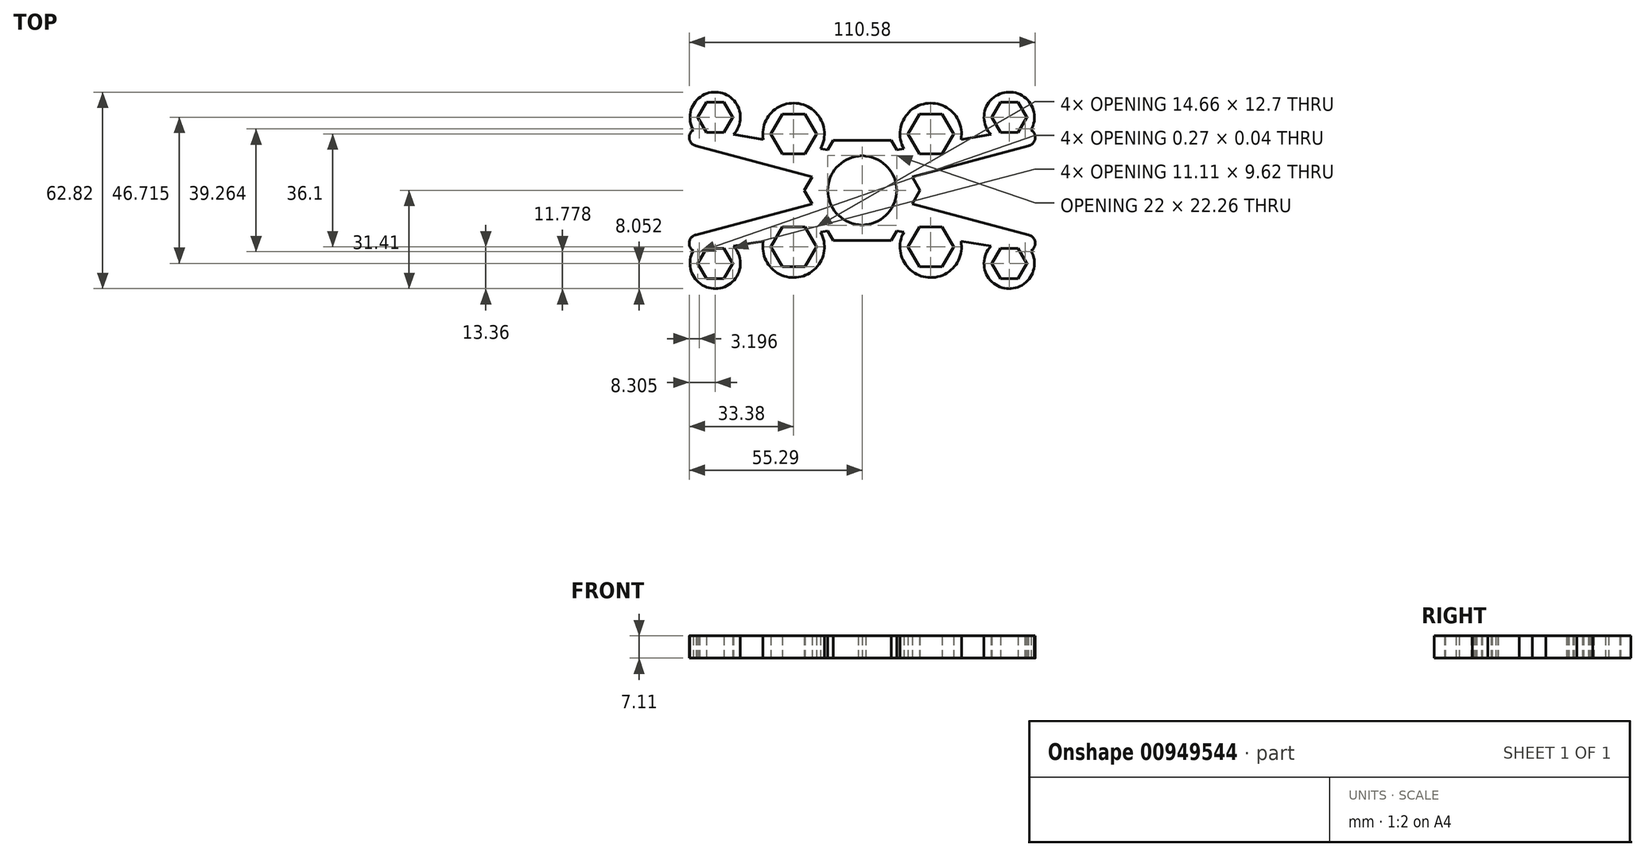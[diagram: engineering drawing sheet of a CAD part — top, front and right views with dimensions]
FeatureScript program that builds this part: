
annotation { "Feature Type Name" : "Feature", "Feature Type Description" : "" }
export const myFeature = defineFeature(function(context is Context, id is Id, definition is map)
    precondition{}
    {
        {
            var Q0;
            Q0=qCreatedBy(makeId("Top.planeOp"),FACE);
            var sketch = newSketch(context, id + "F0", { "sketchPlane" : qUnion([Q0])});
            skCircle(sketch, "E0", {"center": v(0, 0) * mm, "radius": 11 * mm});
            skCircle(sketch, "E1.cCircle", {"center": v(0, 0) * mm, "radius": 16 * mm, "construction": true});
            skLineSegment(sketch, "E1.0", {"start": v(18.48, 0) * mm, "end": v(9.24, -16) * mm});
            skLineSegment(sketch, "E1.1", {"start": v(9.24, -16) * mm, "end": v(-9.24, -16) * mm});
            skLineSegment(sketch, "E1.2", {"start": v(-9.24, -16) * mm, "end": v(-18.48, 0) * mm});
            skLineSegment(sketch, "E1.3", {"start": v(-18.48, 0) * mm, "end": v(-9.24, 16) * mm});
            skLineSegment(sketch, "E1.4", {"start": v(-9.24, 16) * mm, "end": v(9.24, 16) * mm});
            skLineSegment(sketch, "E1.5", {"start": v(9.24, 16) * mm, "end": v(18.48, 0) * mm});
            skPoint(sketch, "E1.0.midPoint", {"position": v(13.86, -8) * mm});
            skLineSegment(sketch, "E2", {"start": v(0, 0) * mm, "end": v(53.37, 14.3) * mm});
            skLineSegment(sketch, "E3", {"start": v(53.37, 14.3) * mm, "end": v(0, 0) * mm});
            skLineSegment(sketch, "E4", {"start": v(18.48, 0) * mm, "end": v(0, 0) * mm, "construction": true});
            skLineSegment(sketch, "E5", {"start": v(56.9, 20.41) * mm, "end": v(-2.32, 10.75) * mm});
            skLineSegment(sketch, "E6", {"start": v(57.96, 15.53) * mm, "end": v(56.9, 20.41) * mm});
            skArc(sketch, "E7", {"start": v(53.13, 14.24) * mm, "mid": v(55.22, 17.5) * mm, "end": v(51.96, 19.6) * mm});
            skCircle(sketch, "E8.cCircle", {"center": v(21.91, 18.05) * mm, "radius": 7.33 * mm, "construction": true});
            skLineSegment(sketch, "E8.0", {"start": v(25.58, 11.7) * mm, "end": v(18.24, 11.7) * mm});
            skLineSegment(sketch, "E8.1", {"start": v(18.24, 11.7) * mm, "end": v(14.58, 18.05) * mm});
            skLineSegment(sketch, "E8.2", {"start": v(14.58, 18.05) * mm, "end": v(18.24, 24.4) * mm});
            skLineSegment(sketch, "E8.3", {"start": v(18.24, 24.4) * mm, "end": v(25.58, 24.4) * mm});
            skLineSegment(sketch, "E8.4", {"start": v(25.58, 24.4) * mm, "end": v(29.24, 18.05) * mm});
            skLineSegment(sketch, "E8.5", {"start": v(29.24, 18.05) * mm, "end": v(25.58, 11.7) * mm});
            skCircle(sketch, "E9.0", {"center": v(21.91, 18.05) * mm, "radius": 9.83 * mm});
            skCircle(sketch, "E10.cCircle", {"center": v(46.99, 23.36) * mm, "radius": 5.56 * mm, "construction": true});
            skLineSegment(sketch, "E10.0", {"start": v(49.76, 18.55) * mm, "end": v(44.2, 18.55) * mm});
            skLineSegment(sketch, "E10.1", {"start": v(44.2, 18.55) * mm, "end": v(41.43, 23.36) * mm});
            skLineSegment(sketch, "E10.2", {"start": v(41.43, 23.36) * mm, "end": v(44.2, 28.17) * mm});
            skLineSegment(sketch, "E10.3", {"start": v(44.2, 28.17) * mm, "end": v(49.76, 28.17) * mm});
            skLineSegment(sketch, "E10.4", {"start": v(49.76, 28.17) * mm, "end": v(52.54, 23.36) * mm});
            skLineSegment(sketch, "E10.5", {"start": v(52.54, 23.36) * mm, "end": v(49.76, 18.55) * mm});
            skCircle(sketch, "E11.0", {"center": v(46.99, 23.36) * mm, "radius": 8.06 * mm});
            skLineSegment(sketch, "E12", {"start": v(0, 16) * mm, "end": v(0, -16) * mm, "construction": true});
            skLineSegment(sketch, "E13", {"start": v(-18.48, 0) * mm, "end": v(18.48, 0) * mm, "construction": true});
            skLineSegment(sketch, "E14.MirrorCS", {"start": v(14.58, -18.05) * mm, "end": v(18.24, -24.4) * mm});
            skLineSegment(sketch, "E15.MirrorCS", {"start": v(18.24, -24.4) * mm, "end": v(25.58, -24.4) * mm});
            skLineSegment(sketch, "E16.MirrorCS", {"start": v(25.58, -24.4) * mm, "end": v(29.24, -18.05) * mm});
            skLineSegment(sketch, "E17.MirrorCS", {"start": v(56.9, -20.41) * mm, "end": v(-2.32, -10.75) * mm});
            skLineSegment(sketch, "E18.MirrorCS", {"start": v(29.24, -18.05) * mm, "end": v(25.58, -11.7) * mm});
            skLineSegment(sketch, "E19.MirrorCS", {"start": v(25.58, -11.7) * mm, "end": v(18.24, -11.7) * mm});
            skLineSegment(sketch, "E20.MirrorCS", {"start": v(18.24, -11.7) * mm, "end": v(14.58, -18.05) * mm});
            skCircle(sketch, "E21.MirrorC", {"center": v(21.91, -18.05) * mm, "radius": 9.83 * mm});
            skLineSegment(sketch, "E22.MirrorCS", {"start": v(0, 0) * mm, "end": v(57.96, -15.53) * mm});
            skArc(sketch, "E23.MirrorCS", {"start": v(53.13, -14.24) * mm, "mid": v(55.22, -17.5) * mm, "end": v(51.96, -19.6) * mm});
            skLineSegment(sketch, "E24.MirrorCS", {"start": v(41.43, -23.36) * mm, "end": v(44.2, -28.17) * mm});
            skLineSegment(sketch, "E25.MirrorCS", {"start": v(44.2, -28.17) * mm, "end": v(49.76, -28.17) * mm});
            skLineSegment(sketch, "E26.MirrorCS", {"start": v(49.76, -28.17) * mm, "end": v(52.54, -23.36) * mm});
            skLineSegment(sketch, "E27.MirrorCS", {"start": v(52.54, -23.36) * mm, "end": v(49.76, -18.55) * mm});
            skCircle(sketch, "E28.MirrorC", {"center": v(46.99, -23.36) * mm, "radius": 5.56 * mm, "construction": true});
            skLineSegment(sketch, "E29.MirrorCS", {"start": v(49.76, -18.55) * mm, "end": v(44.2, -18.55) * mm});
            skLineSegment(sketch, "E30.MirrorCS", {"start": v(44.2, -18.55) * mm, "end": v(41.43, -23.36) * mm});
            skCircle(sketch, "E31.MirrorC", {"center": v(46.99, -23.36) * mm, "radius": 8.06 * mm});
            skLineSegment(sketch, "E32.MirrorCS", {"start": v(-25.58, -11.7) * mm, "end": v(-18.24, -11.7) * mm});
            skLineSegment(sketch, "E33.MirrorCS", {"start": v(-29.24, -18.05) * mm, "end": v(-25.58, -11.7) * mm});
            skLineSegment(sketch, "E34.MirrorCS", {"start": v(-18.24, -11.7) * mm, "end": v(-14.58, -18.05) * mm});
            skLineSegment(sketch, "E35.MirrorCS", {"start": v(-14.58, -18.05) * mm, "end": v(-18.24, -24.4) * mm});
            skLineSegment(sketch, "E36.MirrorCS", {"start": v(-18.24, -24.4) * mm, "end": v(-25.58, -24.4) * mm});
            skLineSegment(sketch, "E37.MirrorCS", {"start": v(-25.58, -24.4) * mm, "end": v(-29.24, -18.05) * mm});
            skCircle(sketch, "E38.MirrorC", {"center": v(-21.91, -18.05) * mm, "radius": 9.83 * mm});
            skLineSegment(sketch, "E39.MirrorCS", {"start": v(-56.9, -20.41) * mm, "end": v(2.32, -10.75) * mm});
            skLineSegment(sketch, "E40.MirrorCS", {"start": v(0, 0) * mm, "end": v(-57.96, -15.53) * mm});
            skLineSegment(sketch, "E41.MirrorCS", {"start": v(-49.76, -18.55) * mm, "end": v(-44.2, -18.55) * mm});
            skLineSegment(sketch, "E42.MirrorCS", {"start": v(-44.2, -18.55) * mm, "end": v(-41.43, -23.36) * mm});
            skLineSegment(sketch, "E43.MirrorCS", {"start": v(-52.54, -23.36) * mm, "end": v(-49.76, -18.55) * mm});
            skCircle(sketch, "E44.MirrorC", {"center": v(-46.99, -23.36) * mm, "radius": 5.56 * mm, "construction": true});
            skLineSegment(sketch, "E45.MirrorCS", {"start": v(-41.43, -23.36) * mm, "end": v(-44.2, -28.17) * mm});
            skLineSegment(sketch, "E46.MirrorCS", {"start": v(-44.2, -28.17) * mm, "end": v(-49.76, -28.17) * mm});
            skLineSegment(sketch, "E47.MirrorCS", {"start": v(-49.76, -28.17) * mm, "end": v(-52.54, -23.36) * mm});
            skArc(sketch, "E48.MirrorCS", {"start": v(-53.13, -14.24) * mm, "mid": v(-55.22, -17.5) * mm, "end": v(-51.96, -19.6) * mm});
            skLineSegment(sketch, "E49.MirrorCS", {"start": v(-18.24, 24.4) * mm, "end": v(-25.58, 24.4) * mm});
            skLineSegment(sketch, "E50.MirrorCS", {"start": v(-14.58, 18.05) * mm, "end": v(-18.24, 24.4) * mm});
            skLineSegment(sketch, "E51.MirrorCS", {"start": v(-18.24, 11.7) * mm, "end": v(-14.58, 18.05) * mm});
            skLineSegment(sketch, "E52.MirrorCS", {"start": v(-25.58, 11.7) * mm, "end": v(-18.24, 11.7) * mm});
            skLineSegment(sketch, "E53.MirrorCS", {"start": v(-29.24, 18.05) * mm, "end": v(-25.58, 11.7) * mm});
            skLineSegment(sketch, "E54.MirrorCS", {"start": v(-25.58, 24.4) * mm, "end": v(-29.24, 18.05) * mm});
            skCircle(sketch, "E55.MirrorC", {"center": v(-21.91, 18.05) * mm, "radius": 9.83 * mm});
            skLineSegment(sketch, "E56.MirrorCS", {"start": v(-56.9, 20.41) * mm, "end": v(2.32, 10.75) * mm});
            skLineSegment(sketch, "E57.MirrorCS", {"start": v(-57.96, 15.53) * mm, "end": v(0, 0) * mm});
            skLineSegment(sketch, "E58.MirrorCS", {"start": v(-44.2, 28.17) * mm, "end": v(-49.76, 28.17) * mm});
            skLineSegment(sketch, "E59.MirrorCS", {"start": v(-49.76, 18.55) * mm, "end": v(-44.2, 18.55) * mm});
            skLineSegment(sketch, "E60.MirrorCS", {"start": v(-52.54, 23.36) * mm, "end": v(-49.76, 18.55) * mm});
            skLineSegment(sketch, "E61.MirrorCS", {"start": v(-44.2, 18.55) * mm, "end": v(-41.43, 23.36) * mm});
            skLineSegment(sketch, "E62.MirrorCS", {"start": v(-41.43, 23.36) * mm, "end": v(-44.2, 28.17) * mm});
            skLineSegment(sketch, "E63.MirrorCS", {"start": v(-49.76, 28.17) * mm, "end": v(-52.54, 23.36) * mm});
            skCircle(sketch, "E64.MirrorC", {"center": v(-46.99, 23.36) * mm, "radius": 8.06 * mm});
            skArc(sketch, "E65.MirrorCS", {"start": v(-53.13, 14.24) * mm, "mid": v(-55.22, 17.5) * mm, "end": v(-51.96, 19.6) * mm});
            skCircle(sketch, "E66.MirrorC", {"center": v(-46.99, -23.36) * mm, "radius": 8.06 * mm});
            skPoint(sketch, "E67.MirrorCS.end.orphan", {"position": v(56.9, -20.41) * mm});
            skPoint(sketch, "E67.MirrorCS.start.orphan", {"position": v(57.96, -15.53) * mm});
            skPoint(sketch, "E68.MirrorCS.end.orphan", {"position": v(-56.9, -20.41) * mm});
            skPoint(sketch, "E68.MirrorCS.start.orphan", {"position": v(-57.96, -15.53) * mm});
            skPoint(sketch, "E69.MirrorCS.end.orphan", {"position": v(-56.9, 20.41) * mm});
            skPoint(sketch, "E69.MirrorCS.start.orphan", {"position": v(-57.96, 15.53) * mm});
            skSolve(sketch);
        }
        {
            var Q0;
            Q0 = qSketchRegion(id + "F0", true);
            extrude(context, id + "F1", {"entities" : qUnion([Q0]), "depth" : 7.11 * mm, "offsetDistance" : 25 * mm});
        }
    });
